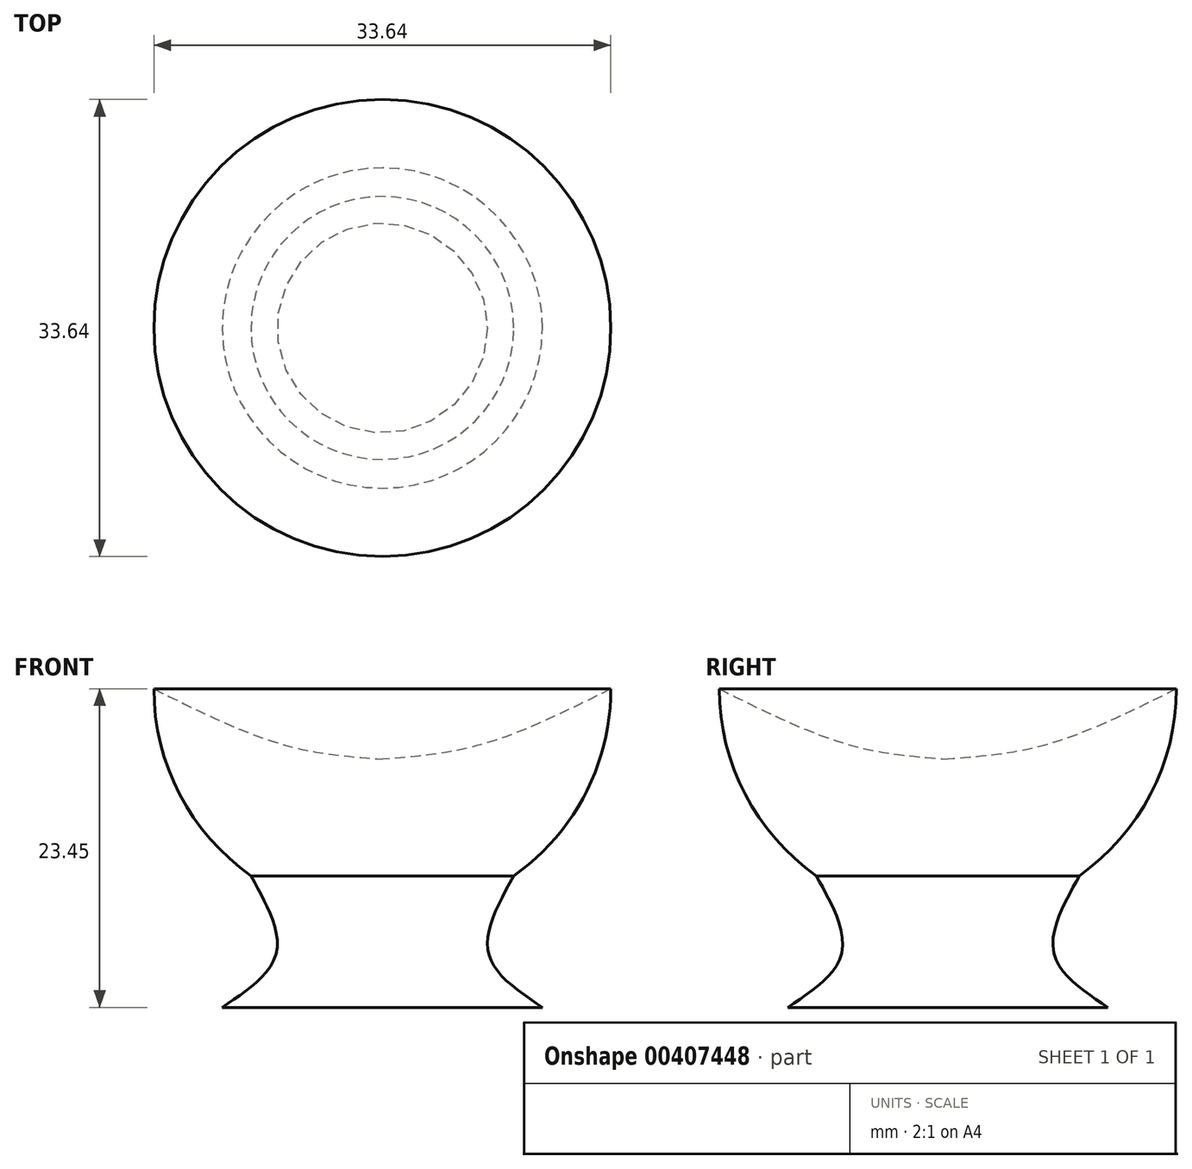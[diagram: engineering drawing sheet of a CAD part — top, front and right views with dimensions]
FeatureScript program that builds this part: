
annotation { "Feature Type Name" : "Feature", "Feature Type Description" : "" }
export const myFeature = defineFeature(function(context is Context, id is Id, definition is map)
    precondition{}
    {
        {
            var Q0;
            Q0=qCreatedBy(makeId("Front.planeOp"),FACE);
            var sketch = newSketch(context, id + "F0", { "sketchPlane" : qUnion([Q0])});
            skFitSpline(sketch, "E0", {"points": [v(16.82, 0) * mm, v(7.29, -4.1) * mm, v(0, -5.17) * mm], "startDerivative": vector(-18.01, -8.99) * mm, "endDerivative": vector(-15.57, -1.12) * mm});
            skLineSegment(sketch, "E1", {"start": v(0, -5.17) * mm, "end": v(0, -16.82) * mm});
            skLineSegment(sketch, "E2", {"start": v(0, -16.82) * mm, "end": v(0, -23.45) * mm});
            skLineSegment(sketch, "E3", {"start": v(0, -23.45) * mm, "end": v(11.79, -23.45) * mm});
            skFitSpline(sketch, "E4", {"points": [v(11.79, -23.45) * mm, v(7.82, -19.47) * mm, v(9.67, -13.76) * mm], "startDerivative": vector(-10.97, 7.3) * mm, "endDerivative": vector(6.64, 12.03) * mm});
            skArc(sketch, "E5", {"start": v(16.82, 0) * mm, "mid": v(14.93, -7.76) * mm, "end": v(9.67, -13.76) * mm});
            skSolve(sketch);
        }
        {
            var Q0;
            Q0=makeQuery(id+"F0.imprint","IMPRINT",FACE,{"disambiguationData":[TD([[makeQuery(id+"F0.imprint","IMPRINT",EDGE,{"derivedFrom":sQuery(id+"F0.wireOp",EDGE,"E0")}),1.0]])]});
            var Q1;
            Q1=sQuery(id+"F0.wireOp",EDGE,"E2");
            revolve(context, id + "F1", {"surfaceOperationType" : NewSurfaceOperationType.NEW, "entities" : qUnion([Q0]), "axis" : qUnion([Q1]), "revolveType" : RevolveType.FULL});
        }
    });
